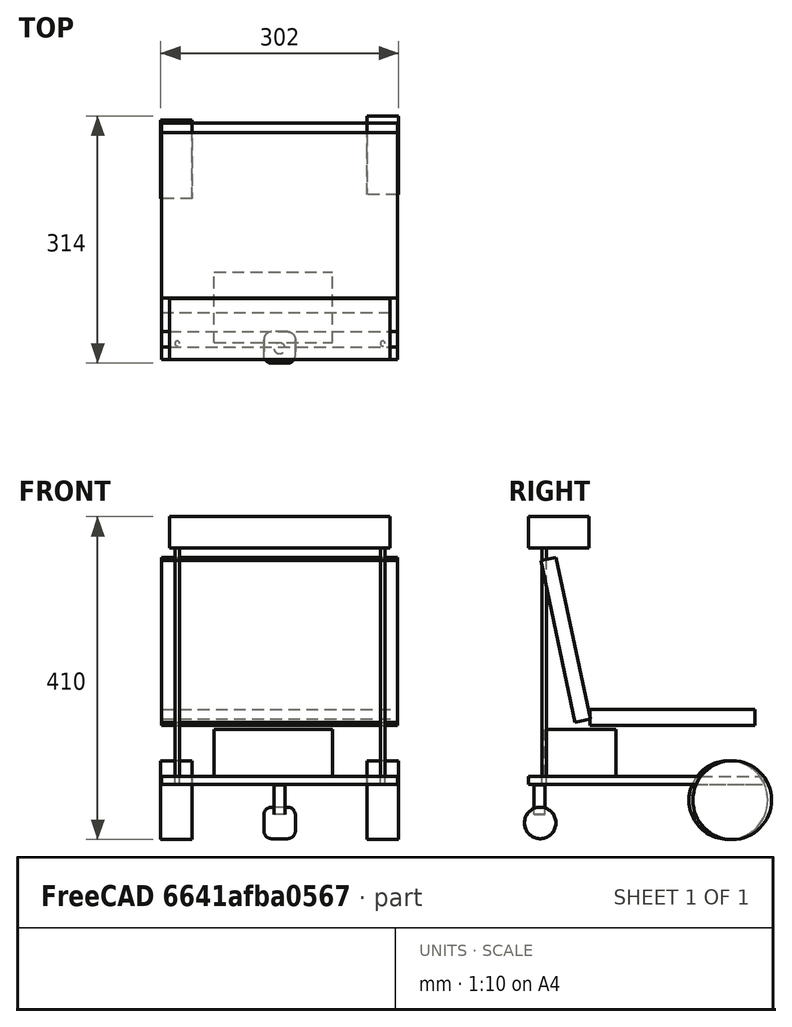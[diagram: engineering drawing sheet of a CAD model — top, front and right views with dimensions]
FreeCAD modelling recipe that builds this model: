
FCSTD DOCUMENT  (FreeCAD 0.14R3702 (Git))
Label: hal
License: CC-BY 3.0
LicenseURL: http://creativecommons.org/licenses/by/3.0/
objects: Part::Cylinder×6, Part::Box×5, Part::Fillet×1
note: 12 computed .brp shape members not serialized (recipe doc carries the construction recipe); baked Part::Feature solids carry a one-line shape summary decoded from their .brp

FEATURE [Part::Box] Box  label="base"
  Height = 10
  Length = 300
  Width = 300
FEATURE [Part::Box] Box001  label="kinect"
  Height = 40
  Length = 280
  Placement = pos=(10,0,300) rot=(0,0,1;0rad)
  Width = 77
FEATURE [Part::Box] Box002  label="battery"
  Height = 60
  Length = 150
  Placement = pos=(67,21,10) rot=(0,0,1;0rad)
  Width = 90
FEATURE [Part::Box] Box003  label="lap_top"
  Height = 20
  Length = 300
  Placement = pos=(0,79,83) rot=(1,0,0;1.78024rad)
  Width = 210
FEATURE [Part::Box] Box004  label="lap+bot"
  Height = 20
  Length = 300
  Placement = pos=(0,78,75) rot=(0,0,1;0rad)
  Width = 210
FEATURE [Part::Cylinder] Cylinder  label="wheel"
  Angle = 360
  Height = 40
  Placement = pos=(39,254,-20) rot=(0,-1,0;1.5708rad)
  Radius = 50
FEATURE [Part::Cylinder] Cylinder001  label="wheel1"
  Angle = 360
  Height = 40
  Placement = pos=(301,259,-20) rot=(0,-1,0;1.5708rad)
  Radius = 50
FEATURE [Part::Cylinder] Cylinder002  label="Cylinder"
  Angle = 360
  Height = 300
  Placement = pos=(20,20,0) rot=(0,0,1;0rad)
  Radius = 3
FEATURE [Part::Cylinder] Cylinder003  label="Cylinder001"
  Angle = 360
  Height = 300
  Placement = pos=(281,20,0) rot=(0,0,1;0rad)
  Radius = 3
FEATURE [Part::Cylinder] Cylinder004  label="wheel002"
  Angle = 360
  Height = 40
  Placement = pos=(170,15,-49) rot=(0,-1,0;1.5708rad)
  Radius = 20
FEATURE [Part::Cylinder] Cylinder006  label="Cylinder003"
  Angle = 360
  Height = 37
  Placement = pos=(150,14,-38) rot=(0,0,1;0rad)
  Radius = 7
FEATURE [Part::Fillet] Fillet
  Base = -> Cylinder004
  Edges = 2 edges r=10: [Edge1,Edge3]
